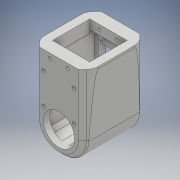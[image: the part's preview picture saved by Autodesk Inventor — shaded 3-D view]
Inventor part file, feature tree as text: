
AUTODESK INVENTOR PART (.ipt)
format: ipt  version: 2018 (Build 220112000, 112)  size: 759,808 bytes
history: native  units: mm
features: sketch x32, projected_geometry x30, extrude x26, hole x8, fillet x6, chamfer x3, mirror x1
ambient origin geometry x8: Origin, YZ Plane, XZ Plane, XY Plane, X Axis, Y Axis, Z Axis, Center Point
bodies: Solid1 (feature_tree)
feature tree (106):
  extrude  "Extrusion1"  Depth=45.0mm
  extrude  "Extrusion2"  Depth=2.25mm
  hole  "Hole1"  [1 undecoded]
  hole  "Hole2"  [1 undecoded]
  fillet  "Fillet1"  Radius=14.0mm
  extrude  "Extrusion3"  Depth=18.5mm
  extrude  "Extrusion4"  Depth=10.0mm
  extrude  "Extrusion5"  Depth=2.0mm
  extrude  "Extrusion6"  Depth=2.0mm
  hole  "Hole3"  [1 undecoded]
  extrude  "Extrusion7"  Depth=0.5mm
  extrude  "Extrusion8"  Depth=5.0mm TaperAngle=0.0deg
  extrude  "Extrusion9"  Depth=10.0mm
  extrude  "Extrusion10"  Depth=10.0mm
  extrude  "Extrusion11"  Depth=14.5mm
  extrude  "Extrusion12"  Depth=14.5mm
  extrude  "Extrusion13"  Depth=5.0mm
  extrude  "Extrusion14"  Depth=2.25mm
  extrude  "Extrusion15"  Depth=5.0mm
  extrude  "Extrusion16"  Depth=9.0mm
  extrude  "Extrusion17"  Depth=4.0mm
  chamfer  "Chamfer1"  Distance=1.0mm
  fillet  "Fillet7"  Radius=20.7mm
  fillet  "Fillet8"  Radius=32.0mm
  mirror  "Mirror1"
  extrude  "Extrusion19"  Depth=1.0mm TaperAngle=0.0deg
  extrude  "Extrusion20"  Depth=8.0mm
  extrude  "Extrusion21"  Depth=0.2mm TaperAngle=0.0deg
  extrude  "Extrusion22"  Depth=0.5mm TaperAngle=0.0deg
  extrude  "Extrusion23"  Depth=5.0mm TaperAngle=0.0deg
  chamfer  "Chamfer2"  Distance=5.0mm
  fillet  "Fillet9"  Radius=0.2mm
  extrude  "Extrusion24"  Depth=2.0mm TaperAngle=45.0deg
  extrude  "Extrusion27"  Depth=0.5mm
  extrude  "Extrusion28"  Depth=1.8mm TaperAngle=0.0deg
  hole  "Hole6"  [1 undecoded]
  sketch  "Sketch39"  dims[d105=1.5mm d114=0.5mm]
  hole  "Hole7"  [1 undecoded]
  hole  "Hole8"  [1 undecoded]
  fillet  "Fillet10"  Radius=2.0mm
  hole  "Hole9"  [1 undecoded]
  extrude  "Extrusion29"  Depth=2.0mm TaperAngle=45.0deg
  chamfer  "Chamfer4"  Distance=8.0mm
  hole  "Hole10"  [1 undecoded]
  fillet  "Fillet11"  Radius=10.0mm
  sketch  "Sketch1"  dims[d0=24.5mm d1=45.0mm]
  sketch  "Sketch2"  dims[d2=1.95mm d3=0.0mm d4=2.25mm]
  projected_geometry  "Projected Loop1"
  sketch  "Sketch3"  dims[d5=20.0mm d6=2.25mm]
  projected_geometry  "Projected Loop2"
  sketch  "Sketch4"  dims[d7=5.25mm d8=5.25mm d9=14.0mm]
  projected_geometry  "Projected Loop3"
  sketch  "Sketch5"  dims[d10=5.25mm d11=18.5mm]
  projected_geometry  "Projected Loop4"
  sketch  "Sketch6"  dims[d12=10.0mm d13=0.0mm d14=20.5mm]
  projected_geometry  "Projected Loop5"
  sketch  "Sketch7"  dims[d15=2.0mm d16=2.195mm]
  projected_geometry  "Projected Loop6"
  sketch  "Sketch8"  dims[d17=2.0mm]
  projected_geometry  "Projected Loop7"
  sketch  "Sketch9"  dims[d18=2.4mm d19=6.0mm d20=4.4mm d21=2.0mm d22=90.0deg d23=8.0mm d24=20.594885mm d25=20.5mm]
  projected_geometry  "Projected Loop8"
  projected_geometry  "Projected Loop9"
  sketch  "Sketch10"  dims[d26=26.65mm d27=2.0mm]
  projected_geometry  "Projected Loop10"
  projected_geometry  "Projected Loop11"
  sketch  "Sketch11"  dims[d28=2.0mm]
  projected_geometry  "Projected Loop12"
  sketch  "Sketch12"  dims[d29=2.4mm d30=6.0mm d31=4.4mm d32=2.0mm d33=90.0deg d34=8.0mm d35=20.594885mm d36=0.5mm]
  sketch  "Sketch13"  dims[d37=18.0mm d38=5.0mm d39=0.0mm]
  sketch  "Sketch14"  dims[d41=10.0mm d42=0.0mm d43=24.5mm]
  projected_geometry  "Projected Loop13"
  sketch  "Sketch15"  dims[d44=1.15mm d45=0.0mm d46=10.0mm]
  sketch  "Sketch16"  dims[d47=21.0mm d48=14.5mm]
  projected_geometry  "Projected Loop14"
  sketch  "Sketch17"  dims[d49=20.0mm d50=14.5mm]
  projected_geometry  "Projected Loop15"
  sketch  "Sketch18"  dims[d51=24.5mm d52=5.0mm]
  projected_geometry  "Projected Loop16"
  sketch  "Sketch19"  dims[d53=5.0mm d54=2.25mm]
  projected_geometry  "Projected Loop17"
  sketch  "Sketch20"  dims[d55=2.25mm d56=5.0mm]
  projected_geometry  "Projected Loop18"
  sketch  "Sketch25"  dims[d57=5.0mm d58=9.0mm]
  projected_geometry  "Projected Loop22"
  sketch  "Sketch26"  dims[d59=14.75mm d60=4.0mm d61=1.0mm d62=0.0mm d63=20.7mm]
  projected_geometry  "Projected Loop23"
  sketch  "Sketch27"  dims[d64=2.4mm d65=6.0mm d66=4.4mm d67=2.0mm d68=90.0deg d69=8.0mm d70=20.594885mm d72=32.0mm]
  projected_geometry  "Projected Loop25"
  sketch  "Sketch29"  dims[d73=5.0mm d74=0.0mm d75=1.0mm d76=0.0mm]
  projected_geometry  "Projected Loop26"
  sketch  "Sketch30"  dims[d77=12.25mm d78=0.0mm d80=8.0mm]
  projected_geometry  "Projected Loop27"
  sketch  "Sketch32"  dims[d81=4.5mm d82=0.0mm d84=0.2mm d85=0.0mm]
  projected_geometry  "Projected Loop28"
  projected_geometry  "Projected Loop29"
  sketch  "Sketch36"  dims[d86=21.0mm d87=0.5mm d88=0.0mm]
  projected_geometry  "Projected Loop33"
  sketch  "Sketch37"  dims[d91=8.0mm d92=0.0mm d93=5.0mm d94=0.0mm d95=5.0mm d96=0.0mm d98=0.2mm d99=0.0mm]
  projected_geometry  "Projected Loop34"
  sketch  "Sketch38"  dims[d100=0.2mm d101=0.0mm d102=2.5mm d103=2.0mm d104=45.0deg]
  projected_geometry  "Projected Loop35"
  sketch  "Sketch41"  dims[d128=1.8mm d129=0.0mm d130=1.8mm d131=0.0mm]
  projected_geometry  "Projected Loop36"
  sketch  "Sketch42"  dims[d133=36.055mm d134=4.2225mm d135=4.2225mm d136=2.0mm d137=0.0mm d138=2.0mm d139=0.0mm d140=2.0mm d141=0.0mm d142=5.0mm d143=2.0mm d144=45.0deg d145=8.0mm d147=33.0mm d148=10.0mm d149=0.0mm d161=20.75mm d162=18.0mm d163=25.0mm d164=0.05mm d165=7.0mm d166=0.0mm d167=1.5mm d168=0.0mm d169=3.0mm d170=12.0mm d171=2.1mm d172=6.0mm d173=6.3mm d174=2.0mm d175=90.0deg d176=8.0mm d177=20.594885mm d178=1.567mm d179=36.0mm d180=4.4mm d181=2.0mm d182=90.0deg d183=36.0mm d184=20.594885mm d185=4.0mm d186=5.029mm d187=4.4mm d188=2.0mm d189=90.0deg d190=15.0mm d191=0.0mm d192=0.5mm d193=2.1mm d194=5.029mm d195=4.4mm d196=2.0mm d197=90.0deg d198=20.75mm d199=0.0mm d200=15.0mm d201=1.5mm d202=0.0mm d203=1.5mm d204=2.0mm d205=45.0deg d206=4.0mm d207=5.029mm d208=4.4mm d209=2.0mm d210=90.0deg d211=2.2mm d212=0.0mm d213=0.75mm]
  projected_geometry  "Projected Loop37"
note: 8 required parameter values undecoded (feature->parameter linkage not recoverable at this tier; creation-order binding heuristic only, values carry confidence <= 0.55)
